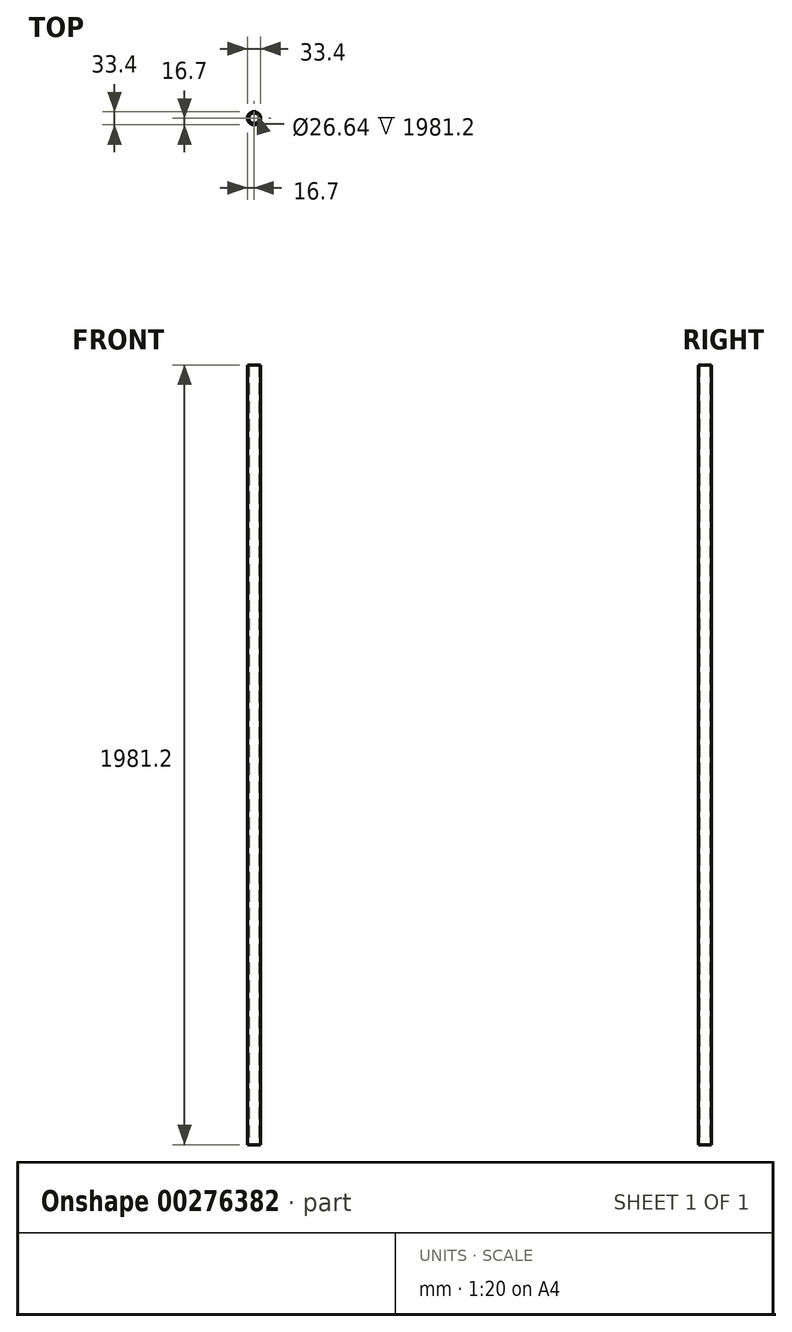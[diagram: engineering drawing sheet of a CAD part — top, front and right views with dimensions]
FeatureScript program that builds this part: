
annotation { "Feature Type Name" : "Feature", "Feature Type Description" : "" }
export const myFeature = defineFeature(function(context is Context, id is Id, definition is map)
    precondition{}
    {
        {
            var Q0;
            Q0=qCreatedBy(makeId("Top.planeOp"),FACE);
            var sketch = newSketch(context, id + "F0", { "sketchPlane" : qUnion([Q0])});
            skCircle(sketch, "E0", {"center": v(0, 0) * mm, "radius": 16.7 * mm});
            skCircle(sketch, "E1", {"center": v(0, 0) * mm, "radius": 13.32 * mm});
            skSolve(sketch);
        }
        {
            var Q0;
            Q0=makeQuery(id+"F0.imprint","IMPRINT",FACE,{"disambiguationData":[TD([[makeQuery(id+"F0.imprint","IMPRINT",EDGE,{"derivedFrom":sQuery(id+"F0.wireOp",EDGE,"E0")}),1.0]])]});
            extrude(context, id + "F1", {"entities" : qUnion([Q0]), "depth" : 1981.2 * mm});
        }
    });
